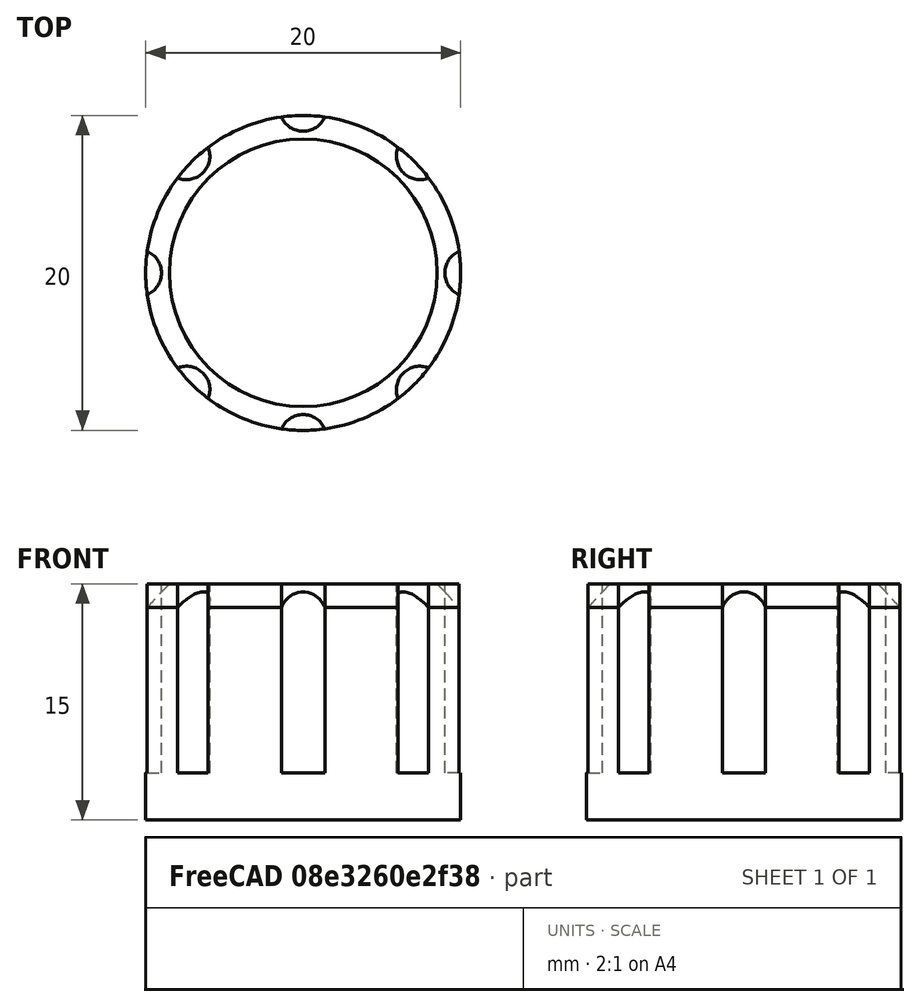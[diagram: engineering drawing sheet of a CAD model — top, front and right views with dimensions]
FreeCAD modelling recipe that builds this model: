
FCSTD DOCUMENT  (FreeCAD 0.18.4R)
Label: tutorial_freecad_ex12_b
License: All rights reserved
LicenseURL: http://en.wikipedia.org/wiki/All_rights_reserved
objects: Part::Cylinder×4, Part::FeaturePython×2, Part::Cut×2, Part::Chamfer×1
note: 9 computed .brp shape members not serialized (recipe doc carries the construction recipe); baked Part::Feature solids carry a one-line shape summary decoded from their .brp

FEATURE [Part::Cylinder] Cylinder  label="base"
  Angle = 360
  AttacherType = Attacher::AttachEngine3D
  Height = 15
  Radius = 10
FEATURE [Part::Cylinder] Cylinder001  label="muesca_master"
  Angle = 360
  AttacherType = Attacher::AttachEngine3D
  Height = 19
  Placement = pos=(10.5,0,3) rot=(0,0,1;0rad)
  Radius = 1.5
FEATURE [Part::FeaturePython] Array  label="muescas"  # Draft array (typed FeaturePython)
  Angle = 360
  ArrayType = 1
  Axis = (0,0,1)
  Base = -> Cylinder001
  Center = (0,0,0)
  Fuse = false
  IntervalAxis = (0,0,0)
  IntervalX = (1,0,0)
  IntervalY = (0,1,0)
  IntervalZ = (0,0,1)
  NumberPolar = 8
  NumberX = 2
  NumberY = 2
  NumberZ = 1
FEATURE [Part::Cut] Cut  label="selector"
  Base = -> Cylinder
  Refine = true
  Tool = -> Array
FEATURE [Part::Cylinder] Cylinder002  label="muesca_master001"
  Angle = 360
  AttacherType = Attacher::AttachEngine3D
  Height = 19
  Placement = pos=(10.5,0,3) rot=(0,0,1;0rad)
  Radius = 1.5
FEATURE [Part::FeaturePython] Array001  label="muescas001"  # Draft array (typed FeaturePython)
  Angle = 360
  ArrayType = 1
  Axis = (0,0,1)
  Base = -> Cylinder002
  Center = (0,0,0)
  Fuse = false
  IntervalAxis = (0,0,0)
  IntervalX = (1,0,0)
  IntervalY = (0,1,0)
  IntervalZ = (0,0,1)
  NumberPolar = 8
  NumberX = 2
  NumberY = 2
  NumberZ = 1
FEATURE [Part::Cylinder] Cylinder003  label="base001"
  Angle = 360
  AttacherType = Attacher::AttachEngine3D
  Height = 15
  Radius = 10
FEATURE [Part::Chamfer] Chamfer
  Base = -> Cylinder003
  Edges = 1 edges r=1.5: [Edge1]
FEATURE [Part::Cut] Cut001  label="selector_nuevo"
  Base = -> Chamfer
  Refine = true
  Tool = -> Array001
